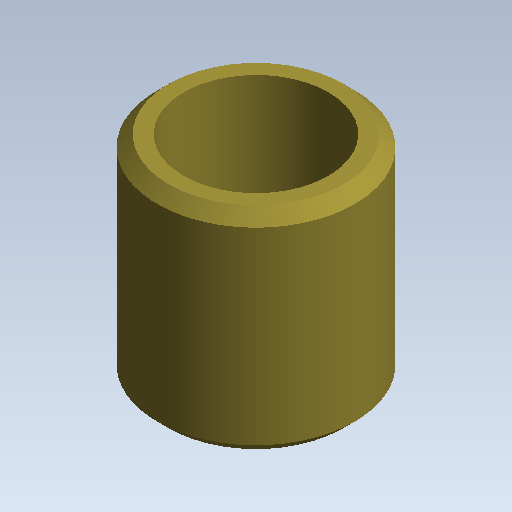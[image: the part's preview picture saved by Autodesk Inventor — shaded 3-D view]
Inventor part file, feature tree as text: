
AUTODESK INVENTOR PART (.ipt)
format: ipt  version: 2020 (Build 240168000, 168)  size: 107,008 bytes
history: native  units: mm (DEFAULTED — no unit token found)
features: other x35, revolve x1, sketch x1
ambient origin geometry x8: Origin, YZ Plane, XZ Plane, XY Plane, X Axis, Y Axis, Z Axis, Center Point
bodies: Solid1 (feature_tree)
feature tree (37):
  revolve  "Revolution1"  [1 undecoded]
  other  "bushing_XY"
  other  "bushing_YZ"
  other  "bushing_ZX"
  other  "bushing_X"
  other  "bushing_Y"
  other  "bushing_Z"
  other  "bushing_Center"
  other  "id1_XY"
  other  "id1_YZ"
  other  "id1_ZX"
  other  "id1_X"
  other  "id1_Y"
  other  "id1_Z"
  other  "id1_Center"
  other  "id2_XY"
  other  "id2_YZ"
  other  "id2_ZX"
  other  "id2_X"
  other  "id2_Y"
  other  "id2_Z"
  other  "id2_Center"
  other  "id3_XY"
  other  "id3_YZ"
  other  "id3_ZX"
  other  "id3_X"
  other  "id3_Y"
  other  "id3_Z"
  other  "id3_Center"
  other  "id4_XY"
  other  "id4_YZ"
  other  "id4_ZX"
  other  "id4_X"
  other  "id4_Y"
  other  "id4_Z"
  other  "id4_Center"
  sketch  "Sketch_1"  dims[d0=360.0deg d1=0.0mm d2=0.0mm]
note: 1 required parameter value undecoded (feature->parameter linkage not recoverable at this tier; creation-order binding heuristic only, values carry confidence <= 0.55)
